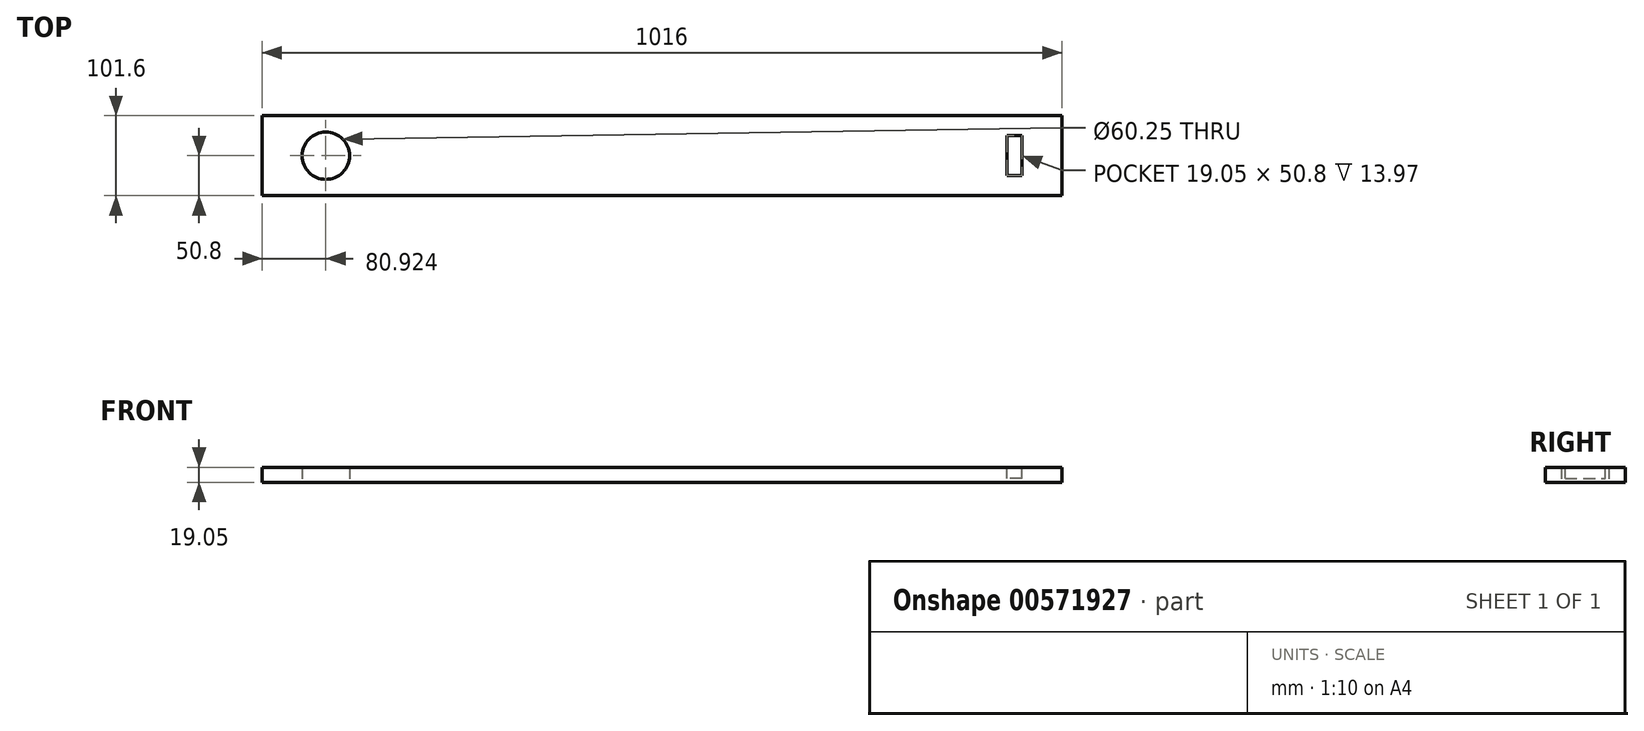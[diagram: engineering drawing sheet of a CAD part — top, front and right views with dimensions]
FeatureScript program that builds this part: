
annotation { "Feature Type Name" : "Feature", "Feature Type Description" : "" }
export const myFeature = defineFeature(function(context is Context, id is Id, definition is map)
    precondition{}
    {
        {
            var Q0;
            Q0=qCreatedBy(makeId("Top.planeOp"),FACE);
            var sketch = newSketch(context, id + "F0", { "sketchPlane" : qUnion([Q0])});
            skLineSegment(sketch, "E0.bottom", {"start": v(0, 0) * mm, "end": v(-1016, 0) * mm});
            skLineSegment(sketch, "E0.top", {"start": v(0, -101.6) * mm, "end": v(-1016, -101.6) * mm});
            skLineSegment(sketch, "E0.left", {"start": v(0, 0) * mm, "end": v(0, -101.6) * mm});
            skLineSegment(sketch, "E0.right", {"start": v(-1016, 0) * mm, "end": v(-1016, -101.6) * mm});
            skCircle(sketch, "E1", {"center": v(-935.08, -50.8) * mm, "radius": 30.12 * mm});
            skSolve(sketch);
        }
        {
            var Q0;
            Q0 = qSketchRegion(id + "F0", true);
            extrude(context, id + "F1", {"entities" : qUnion([Q0]), "depth" : 19.05 * mm, "offsetDistance" : 25.4 * mm});
        }
        {
            var Q0;
            Q0=makeQuery(id+"F1.opExtrude","CAP_FACE",FACE,{"disambiguationData":[OSD([sQuery(id+"F0.wireOp",EDGE,"E0.bottom"),sQuery(id+"F0.wireOp",EDGE,"E0.top"),sQuery(id+"F0.wireOp",EDGE,"E0.left"),sQuery(id+"F0.wireOp",EDGE,"E0.right"),sQuery(id+"F0.wireOp",EDGE,"E1")])],"isStart":false});
            var sketch = newSketch(context, id + "F2", { "sketchPlane" : qUnion([Q0])});
            skLineSegment(sketch, "E2.bottom", {"start": v(-50.8, -76.2) * mm, "end": v(-69.85, -76.2) * mm});
            skLineSegment(sketch, "E2.top", {"start": v(-50.8, -25.4) * mm, "end": v(-69.85, -25.4) * mm});
            skLineSegment(sketch, "E2.left", {"start": v(-50.8, -76.2) * mm, "end": v(-50.8, -25.4) * mm});
            skLineSegment(sketch, "E2.right", {"start": v(-69.85, -76.2) * mm, "end": v(-69.85, -25.4) * mm});
            skSolve(sketch);
        }
        {
            var Q0;
            Q0=makeQuery(id+"F2.imprint","IMPRINT",FACE,{"disambiguationData":[TD([[makeQuery(id+"F2.imprint","IMPRINT",EDGE,{"derivedFrom":sQuery(id+"F2.wireOp",EDGE,"E2.bottom")}),-1.0]])]});
            extrude(context, id + "F3", {"entities" : qUnion([Q0]), "operationType" : NewBodyOperationType.REMOVE, "oppositeDirection" : true, "depth" : 13.97 * mm, "offsetDistance" : 25.4 * mm});
        }
    });
